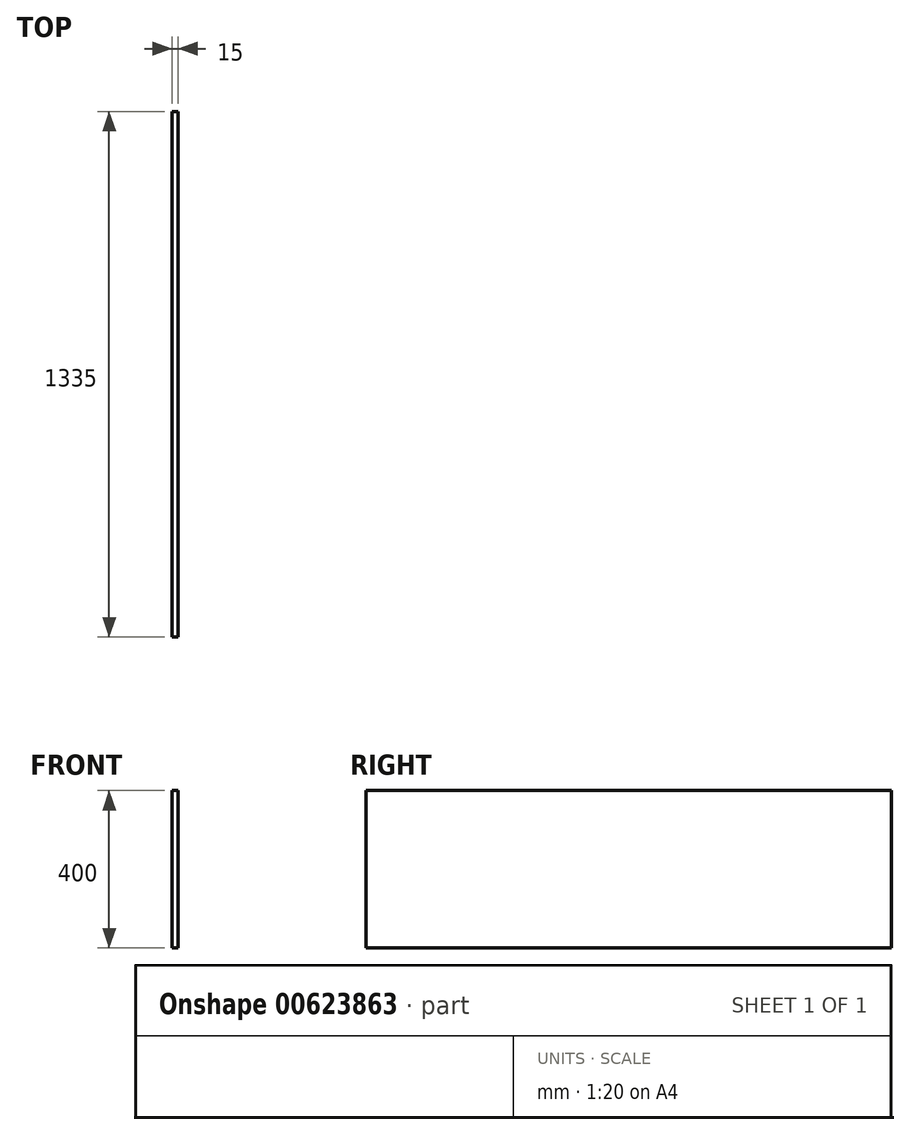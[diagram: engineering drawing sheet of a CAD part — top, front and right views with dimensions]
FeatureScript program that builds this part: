
annotation { "Feature Type Name" : "Feature", "Feature Type Description" : "" }
export const myFeature = defineFeature(function(context is Context, id is Id, definition is map)
    precondition{}
    {
        {
            var Q0;
            Q0=qCreatedBy(makeId("Top.planeOp"),FACE);
            var sketch = newSketch(context, id + "F0", { "sketchPlane" : qUnion([Q0])});
            skLineSegment(sketch, "E0.bottom", {"start": v(0, 1335) * mm, "end": v(15, 1335) * mm});
            skLineSegment(sketch, "E0.top", {"start": v(0, 0) * mm, "end": v(15, 0) * mm});
            skLineSegment(sketch, "E0.left", {"start": v(0, 1335) * mm, "end": v(0, 0) * mm});
            skLineSegment(sketch, "E0.right", {"start": v(15, 1335) * mm, "end": v(15, 0) * mm});
            skSolve(sketch);
        }
        {
            var Q0;
            Q0=qSketchRegion(id+"F0",true);
            extrude(context, id + "F1", {"entities" : qUnion([Q0]), "depth" : 400 * mm, "offsetDistance" : 25 * mm});
        }
    });
